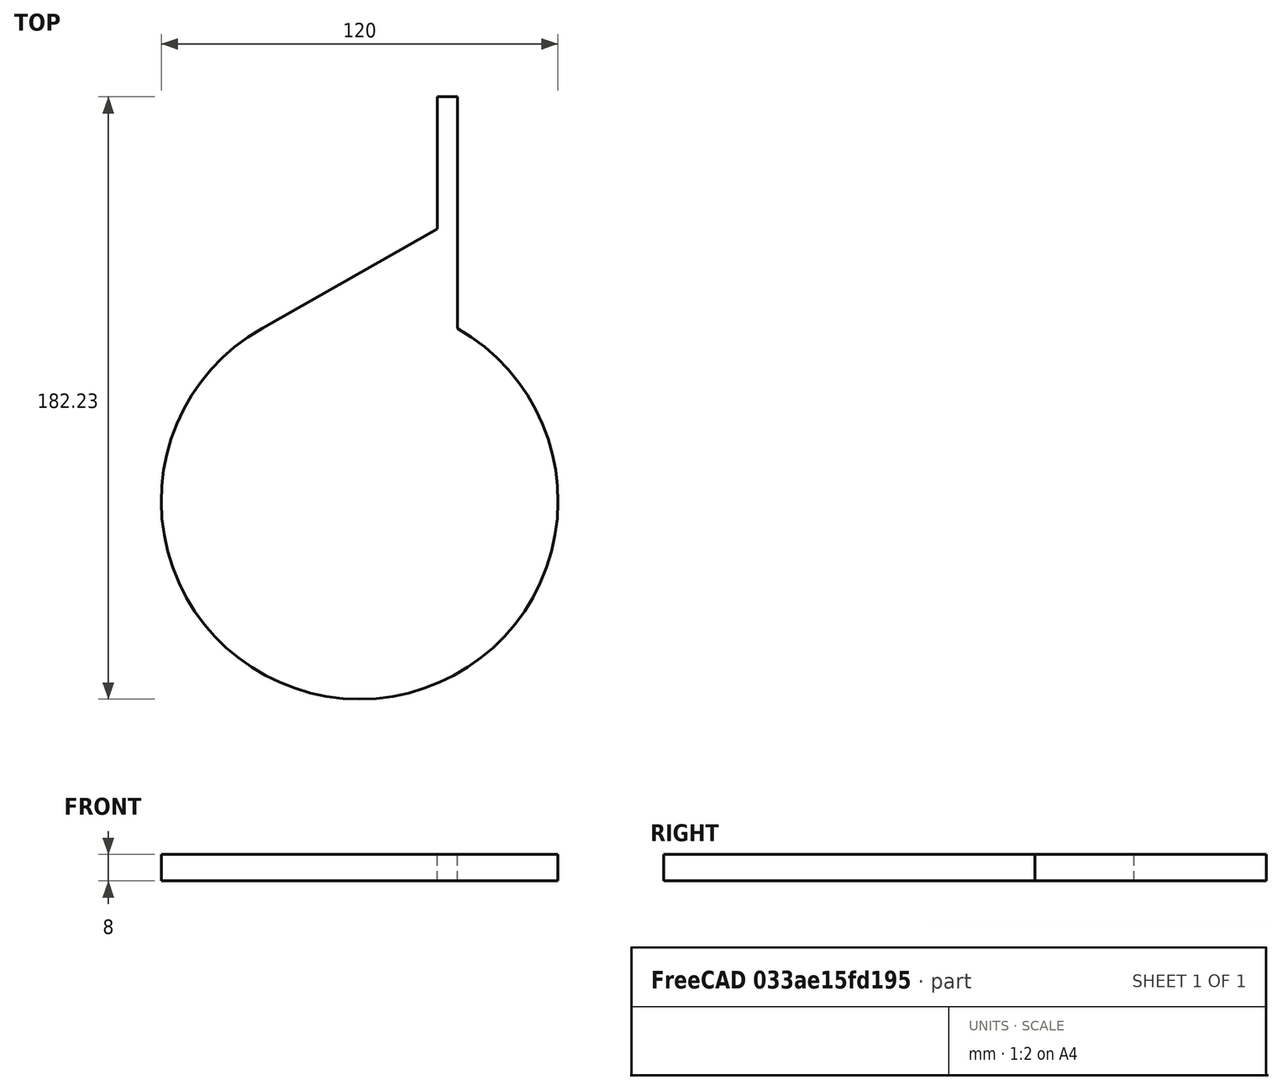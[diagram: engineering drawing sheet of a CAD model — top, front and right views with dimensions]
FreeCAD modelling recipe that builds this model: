
FCSTD DOCUMENT  (FreeCAD 0.14R3702 (Git))
Label: soporte_laser_tube
License: CC-BY 3.0
LicenseURL: http://creativecommons.org/licenses/by/3.0/
objects: Sketcher::SketchObject×1, PartDesign::Pad×1
note: 3 computed .brp shape members not serialized (recipe doc carries the construction recipe); baked Part::Feature solids carry a one-line shape summary decoded from their .brp

FEATURE [Sketcher::SketchObject] Sketch
  sketch-geometry (6):
    g0: ArcOfCircle CenterX=0 CenterY=0 CenterZ=0 NormalX=0 NormalY=0 NormalZ=1 Radius=60 StartAngle=2.08538 EndAngle=7.3394
    g1: LineSegment StartX=23.5303 StartY=122.23 StartZ=0 EndX=29.5303 EndY=122.23 EndZ=0
    g2: LineSegment [constr] StartX=-29.5303 StartY=52.2299 StartZ=0 EndX=29.5303 EndY=52.2299 EndZ=0
    g3: LineSegment StartX=29.5303 StartY=122.23 StartZ=0 EndX=29.5303 EndY=52.2299 EndZ=0
    g4: LineSegment StartX=23.5303 StartY=122.23 StartZ=0 EndX=23.5303 EndY=82.2299 EndZ=0
    g5: LineSegment StartX=23.5303 StartY=82.2299 StartZ=0 EndX=-29.5303 EndY=52.2299 EndZ=0
  constraints (18):
    c: Coincident(g0,g-1)
    c: Radius(g0) = 60
    c: Horizontal(g1)
    c: Distance(g1) = 6
    c: Horizontal(g2)
    c: Coincident(g3,g1)
    c: Vertical(g3)
    c: PointOnObject(g3,g0)
    c: Coincident(g4,g1)
    c: Vertical(g4)
    c: Distance(g4) = 40
    c: Distance(g3) = 70
    c: Coincident(g0,g2)
    c: Coincident(g0,g2)
    c: Coincident(g5,g4)
    c: Coincident(g5,g0)
    c: Tangent(g5,g0)
    c: Coincident(g3,g0)
FEATURE [PartDesign::Pad] Pad
  Length = 8
  Length2 = 100
  Sketch = -> Sketch
  Type = 0
